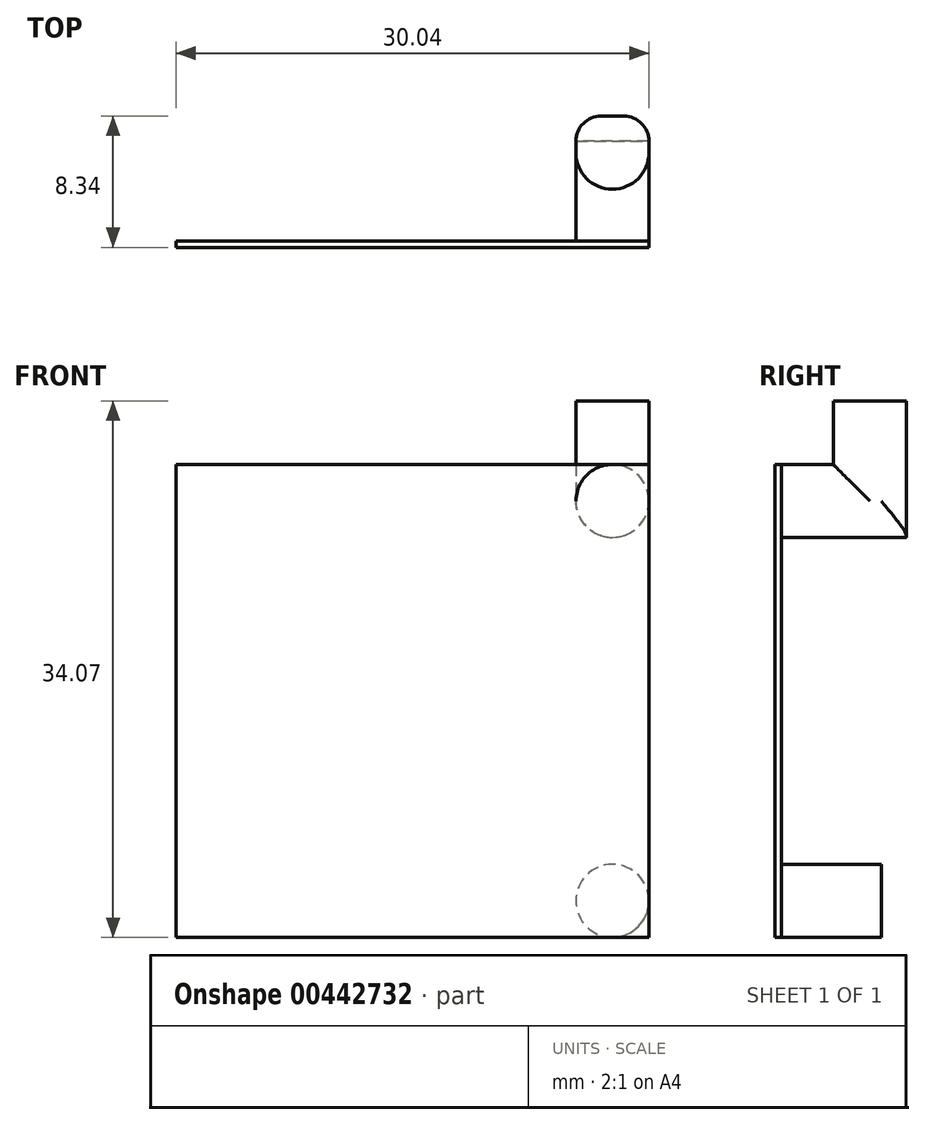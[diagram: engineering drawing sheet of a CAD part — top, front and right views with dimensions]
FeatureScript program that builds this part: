
annotation { "Feature Type Name" : "Feature", "Feature Type Description" : "" }
export const myFeature = defineFeature(function(context is Context, id is Id, definition is map)
    precondition{}
    {
        {
            var Q0;
            Q0=qCreatedBy(makeId("Front.planeOp"),FACE);
            var sketch = newSketch(context, id + "F0", { "sketchPlane" : qUnion([Q0])});
            skLineSegment(sketch, "E0.bottom", {"start": v(12.7, 12.7) * mm, "end": v(-12.7, 12.7) * mm, "construction": true});
            skLineSegment(sketch, "E0.top", {"start": v(12.7, -12.7) * mm, "end": v(-12.7, -12.7) * mm, "construction": true});
            skLineSegment(sketch, "E0.left", {"start": v(12.7, 12.7) * mm, "end": v(12.7, -12.7) * mm, "construction": true});
            skLineSegment(sketch, "E0.right", {"start": v(-12.7, 12.7) * mm, "end": v(-12.7, -12.7) * mm, "construction": true});
            skPoint(sketch, "E0.middle", {"position": v(0, 0) * mm});
            skCircle(sketch, "E1", {"center": v(-12.7, 12.7) * mm, "radius": 2.32 * mm});
            skCircle(sketch, "E2", {"center": v(12.7, 12.7) * mm, "radius": 2.32 * mm});
            skCircle(sketch, "E3", {"center": v(12.7, -12.7) * mm, "radius": 2.32 * mm});
            skCircle(sketch, "E4", {"center": v(-12.7, -12.7) * mm, "radius": 2.32 * mm});
            skLineSegment(sketch, "E5.bottom", {"start": v(-15.02, 15.02) * mm, "end": v(15.02, 15.02) * mm});
            skLineSegment(sketch, "E5.top", {"start": v(-15.02, -15.02) * mm, "end": v(15.02, -15.02) * mm});
            skLineSegment(sketch, "E5.left", {"start": v(-15.02, 15.02) * mm, "end": v(-15.02, -15.02) * mm});
            skLineSegment(sketch, "E5.right", {"start": v(15.02, 15.02) * mm, "end": v(15.02, -15.02) * mm});
            skPoint(sketch, "E6", {"position": v(12.7, 10.38) * mm});
            skSolve(sketch);
        }
        {
            var Q0;
            {var subQ11=sQuery(id+"F0.wireOp",EDGE,"E1");var subQ13=sQuery(id+"F0.wireOp",EDGE,"E5.bottom");var subQ15=makeQuery(id+"F0.imprint","INTERSECT",VERTEX,{"derivedFrom":[subQ11,subQ13]});Q0=makeQuery(id+"F0.imprint","IMPRINT",FACE,{"disambiguationData":[TD([[makeQuery(id+"F0.imprint","IMPRINT",EDGE,{"disambiguationData":[TD([[subQ15,1.0]])],"derivedFrom":subQ11}),-1.0]])]});}
            var Q1;
            {var subQ0=sQuery(id+"F0.wireOp",EDGE,"E4");var subQ1=makeQuery(id+"F0.imprint","INTERSECT",VERTEX,{"derivedFrom":[subQ0,sQuery(id+"F0.wireOp",EDGE,"E5.top")]});Q1=makeQuery(id+"F0.imprint","IMPRINT",FACE,{"disambiguationData":[TD([[makeQuery(id+"F0.imprint","IMPRINT",EDGE,{"disambiguationData":[TD([[subQ1,1.0]])],"derivedFrom":subQ0}),1.0]])]});}
            var Q2;
            {var subQ0=sQuery(id+"F0.wireOp",EDGE,"E1");var subQ1=makeQuery(id+"F0.imprint","INTERSECT",VERTEX,{"derivedFrom":[subQ0,sQuery(id+"F0.wireOp",EDGE,"E5.bottom")]});Q2=makeQuery(id+"F0.imprint","IMPRINT",FACE,{"disambiguationData":[TD([[makeQuery(id+"F0.imprint","IMPRINT",EDGE,{"disambiguationData":[TD([[subQ1,-1.0]])],"derivedFrom":subQ0}),1.0]])]});}
            var Q3;
            {var subQ0=sQuery(id+"F0.wireOp",EDGE,"E2");var subQ1=makeQuery(id+"F0.imprint","INTERSECT",VERTEX,{"derivedFrom":[subQ0,sQuery(id+"F0.wireOp",EDGE,"E5.bottom")]});Q3=makeQuery(id+"F0.imprint","IMPRINT",FACE,{"disambiguationData":[TD([[makeQuery(id+"F0.imprint","IMPRINT",EDGE,{"disambiguationData":[TD([[subQ1,1.0]])],"derivedFrom":subQ0}),1.0]])]});}
            var Q4;
            {var subQ0=sQuery(id+"F0.wireOp",EDGE,"E3");var subQ1=makeQuery(id+"F0.imprint","INTERSECT",VERTEX,{"derivedFrom":[subQ0,sQuery(id+"F0.wireOp",EDGE,"E5.top")]});Q4=makeQuery(id+"F0.imprint","IMPRINT",FACE,{"disambiguationData":[TD([[makeQuery(id+"F0.imprint","IMPRINT",EDGE,{"disambiguationData":[TD([[subQ1,1.0]])],"derivedFrom":subQ0}),1.0]])]});}
            var Q5;
            {var subQ0=sQuery(id+"F0.wireOp",EDGE,"E5.bottom");var subQ1=sQuery(id+"F0.wireOp",EDGE,"E1");var subQ2=makeQuery(id+"F0.imprint","INTERSECT",VERTEX,{"derivedFrom":[subQ1,subQ0]});Q5=makeQuery(id+"F0.imprint","IMPRINT",FACE,{"disambiguationData":[TD([[makeQuery(id+"F0.imprint","IMPRINT",EDGE,{"disambiguationData":[TD([[subQ2,-1.0]])],"derivedFrom":subQ1}),-1.0]])]});}
            var Q6;
            {var subQ0=sQuery(id+"F0.wireOp",EDGE,"E5.bottom");var subQ1=sQuery(id+"F0.wireOp",EDGE,"E2");var subQ2=makeQuery(id+"F0.imprint","INTERSECT",VERTEX,{"derivedFrom":[subQ1,subQ0]});Q6=makeQuery(id+"F0.imprint","IMPRINT",FACE,{"disambiguationData":[TD([[makeQuery(id+"F0.imprint","IMPRINT",EDGE,{"disambiguationData":[TD([[subQ2,1.0]])],"derivedFrom":subQ1}),-1.0]])]});}
            var Q7;
            {var subQ0=sQuery(id+"F0.wireOp",EDGE,"E5.top");var subQ1=sQuery(id+"F0.wireOp",EDGE,"E3");var subQ2=makeQuery(id+"F0.imprint","INTERSECT",VERTEX,{"derivedFrom":[subQ1,subQ0]});Q7=makeQuery(id+"F0.imprint","IMPRINT",FACE,{"disambiguationData":[TD([[makeQuery(id+"F0.imprint","IMPRINT",EDGE,{"disambiguationData":[TD([[subQ2,-1.0]])],"derivedFrom":subQ1}),-1.0]])]});}
            var Q8;
            {var subQ0=sQuery(id+"F0.wireOp",EDGE,"E5.top");var subQ1=sQuery(id+"F0.wireOp",EDGE,"E4");var subQ2=makeQuery(id+"F0.imprint","INTERSECT",VERTEX,{"derivedFrom":[subQ1,subQ0]});Q8=makeQuery(id+"F0.imprint","IMPRINT",FACE,{"disambiguationData":[TD([[makeQuery(id+"F0.imprint","IMPRINT",EDGE,{"disambiguationData":[TD([[subQ2,1.0]])],"derivedFrom":subQ1}),-1.0]])]});}
            extrude(context, id + "F1", {"entities" : qUnion([Q0, Q1, Q2, Q3, Q4, Q5, Q6, Q7, Q8]), "depth" : 0.4 * mm});
        }
        {
            var Q0;
            {var subQ0=sQuery(id+"F0.wireOp",EDGE,"E3");var subQ1=makeQuery(id+"F0.imprint","INTERSECT",VERTEX,{"derivedFrom":[subQ0,sQuery(id+"F0.wireOp",EDGE,"E5.top")]});Q0=makeQuery(id+"F0.imprint","IMPRINT",FACE,{"disambiguationData":[TD([[makeQuery(id+"F0.imprint","IMPRINT",EDGE,{"disambiguationData":[TD([[subQ1,1.0]])],"derivedFrom":subQ0}),1.0]])]});}
            extrude(context, id + "F2", {"entities" : qUnion([Q0]), "operationType" : NewBodyOperationType.ADD, "oppositeDirection" : true, "depth" : 6.35 * mm});
        }
        {
            var Q0;
            Q0=qCreatedBy(makeId("Top.planeOp"),FACE);
            var Q1;
            Q1=sQuery(id+"F0.wireOp",VERTEX,"E2.center");
            cPlane(context, id + "F3", {"entities" : qUnion([Q0, Q1]), "cplaneType" : CPlaneType.PLANE_POINT, "offset" : 25.4 * mm, "width" : 152.4 * mm, "height" : 152.4 * mm});
        }
        {
            var Q0;
            {var subQ0=sQuery(id+"F0.wireOp",EDGE,"E2");var subQ1=makeQuery(id+"F0.imprint","INTERSECT",VERTEX,{"derivedFrom":[subQ0,sQuery(id+"F0.wireOp",EDGE,"E5.bottom")]});Q0=makeQuery(id+"F0.imprint","IMPRINT",FACE,{"disambiguationData":[TD([[makeQuery(id+"F0.imprint","IMPRINT",EDGE,{"disambiguationData":[TD([[subQ1,1.0]])],"derivedFrom":subQ0}),1.0]])]});}
            extrude(context, id + "F4", {"entities" : qUnion([Q0]), "operationType" : NewBodyOperationType.ADD, "oppositeDirection" : true, "depth" : 7.94 * mm});
        }
        {
            var Q0;
            Q0=qCreatedBy(id+"F3.planeOp",FACE);
            var sketch = newSketch(context, id + "F5", { "sketchPlane" : qUnion([Q0])});
            skLineSegment(sketch, "E7.0", {"start": v(15.02, 7.94) * mm, "end": v(10.38, 7.94) * mm});
            skLineSegment(sketch, "E8", {"start": v(12.7, 7.94) * mm, "end": v(12.7, 0) * mm, "construction": true});
            skLineSegment(sketch, "E9", {"start": v(15.02, 7.94) * mm, "end": v(15.02, 5.62) * mm});
            skLineSegment(sketch, "E10", {"start": v(10.38, 7.94) * mm, "end": v(10.38, 5.62) * mm});
            skPoint(sketch, "E11.orphan", {"position": v(15.02, 0) * mm});
            skArc(sketch, "E12", {"start": v(15.02, 5.62) * mm, "mid": v(12.7, 7.94) * mm, "end": v(10.38, 5.62) * mm, "construction": true});
            skArc(sketch, "E13", {"start": v(10.38, 5.62) * mm, "mid": v(12.7, 3.3) * mm, "end": v(15.02, 5.62) * mm});
            skSolve(sketch);
        }
        {
            var Q0;
            Q0=makeQuery(id+"F5.imprint","IMPRINT",FACE,{"disambiguationData":[TD([[makeQuery(id+"F5.imprint","IMPRINT",EDGE,{"derivedFrom":sQuery(id+"F5.wireOp",EDGE,"E7.0")}),1.0]])]});
            extrude(context, id + "F6", {"entities" : qUnion([Q0]), "operationType" : NewBodyOperationType.ADD, "depth" : 6.35 * mm});
        }
        {
            var Q0;
            Q0=makeQuery(id+"F6.opExtrude","SWEPT_EDGE",EDGE,{"disambiguationData":[OSD([sQuery(id+"F5.wireOp",EDGE,"E7.0"),sQuery(id+"F5.wireOp",EDGE,"E9")])]});
            var Q1;
            Q1=makeQuery(id+"F6.opExtrude","SWEPT_EDGE",EDGE,{"disambiguationData":[OSD([sQuery(id+"F5.wireOp",EDGE,"E7.0"),sQuery(id+"F5.wireOp",EDGE,"E10")])]});
            fillet(context, id + "F7", {"entities" : qUnion([Q0, Q1]), "radius" : 1.59 * mm, "allowEdgeOverflow" : false});
        }
    });
